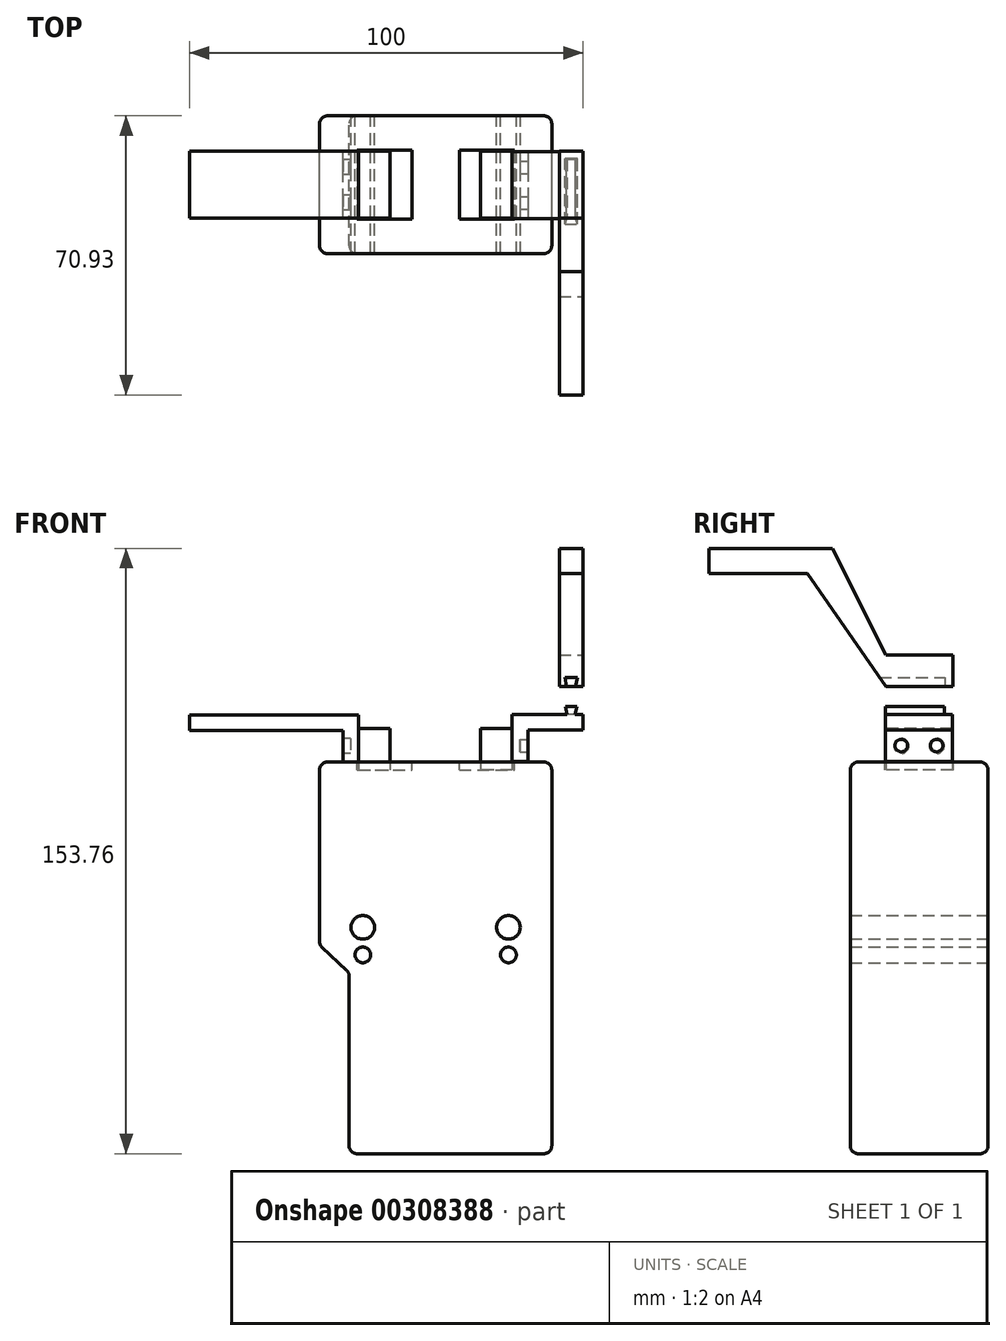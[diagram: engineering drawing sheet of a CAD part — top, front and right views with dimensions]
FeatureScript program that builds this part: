
annotation { "Feature Type Name" : "Feature", "Feature Type Description" : "" }
export const myFeature = defineFeature(function(context is Context, id is Id, definition is map)
    precondition{}
    {
        {
            var Q0;
            Q0=qCreatedBy(makeId("Front.planeOp"),FACE);
            var sketch = newSketch(context, id + "F0", { "sketchPlane" : qUnion([Q0])});
            skLineSegment(sketch, "E0", {"start": v(0, 2) * mm, "end": v(0, 97.5) * mm});
            skLineSegment(sketch, "E1", {"start": v(-2, 99.5) * mm, "end": v(-57, 99.5) * mm});
            skLineSegment(sketch, "E2", {"start": v(-59, 97.5) * mm, "end": v(-59, 53.87) * mm});
            skLineSegment(sketch, "E3", {"start": v(-58.36, 52.4) * mm, "end": v(-52.14, 46.6) * mm});
            skLineSegment(sketch, "E4", {"start": v(-51.5, 45.13) * mm, "end": v(-51.5, 2) * mm});
            skLineSegment(sketch, "E5", {"start": v(-49.5, 0) * mm, "end": v(-2, 0) * mm});
            skCircle(sketch, "E6", {"center": v(-48, 57.5) * mm, "radius": 3 * mm});
            skCircle(sketch, "E7", {"center": v(-48, 50.5) * mm, "radius": 2 * mm});
            skCircle(sketch, "E8", {"center": v(-11, 57.5) * mm, "radius": 3 * mm});
            skCircle(sketch, "E9", {"center": v(-11, 50.5) * mm, "radius": 2 * mm});
            skLineSegment(sketch, "E10", {"start": v(-48, 57.5) * mm, "end": v(-11, 57.5) * mm, "construction": true});
            skLineSegment(sketch, "E11", {"start": v(-48, 50.5) * mm, "end": v(-11, 50.5) * mm, "construction": true});
            skPoint(sketch, "E12.visualSharp", {"position": v(-59, 53) * mm});
            skArc(sketch, "E12.filletArc", {"start": v(-59, 53.87) * mm, "mid": v(-58.83, 53.07) * mm, "end": v(-58.36, 52.4) * mm});
            skPoint(sketch, "E13.visualSharp", {"position": v(-51.5, 46) * mm});
            skArc(sketch, "E13.filletArc", {"start": v(-51.5, 45.13) * mm, "mid": v(-51.67, 45.93) * mm, "end": v(-52.14, 46.6) * mm});
            skPoint(sketch, "E14.visualSharp", {"position": v(-59, 99.5) * mm});
            skArc(sketch, "E14.filletArc", {"start": v(-57, 99.5) * mm, "mid": v(-58.41, 98.91) * mm, "end": v(-59, 97.5) * mm});
            skPoint(sketch, "E15.visualSharp", {"position": v(0, 99.5) * mm});
            skArc(sketch, "E15.filletArc", {"start": v(0, 97.5) * mm, "mid": v(-0.59, 98.91) * mm, "end": v(-2, 99.5) * mm});
            skPoint(sketch, "E16.visualSharp", {"position": v(0, 0) * mm});
            skArc(sketch, "E16.filletArc", {"start": v(-2, 0) * mm, "mid": v(-0.59, 0.59) * mm, "end": v(0, 2) * mm});
            skPoint(sketch, "E17.visualSharp", {"position": v(-51.5, 0) * mm});
            skArc(sketch, "E17.filletArc", {"start": v(-51.5, 2) * mm, "mid": v(-50.91, 0.59) * mm, "end": v(-49.5, 0) * mm});
            skSolve(sketch);
        }
        {
            var Q0;
            Q0=makeQuery(id+"F0.imprint","IMPRINT",FACE,{"disambiguationData":[TD([[makeQuery(id+"F0.imprint","IMPRINT",EDGE,{"derivedFrom":sQuery(id+"F0.wireOp",EDGE,"E0")}),1.0]])]});
            extrude(context, id + "F1", {"entities" : qUnion([Q0]), "depth" : 35 * mm});
        }
        {
            var Q0;
            Q0=makeQuery(id+"F1.opExtrude","CAP_EDGE",EDGE,{"disambiguationData":[OSD([sQuery(id+"F0.wireOp",EDGE,"E0")])],"isStart":true});
            var Q1;
            Q1=makeQuery(id+"F1.opExtrude","CAP_EDGE",EDGE,{"disambiguationData":[OSD([sQuery(id+"F0.wireOp",EDGE,"E1")])],"isStart":false});
            fillet(context, id + "F2", {"entities" : qUnion([Q0, Q1]), "radius" : 2 * mm, "tangentPropagation" : true, "allowEdgeOverflow" : false});
        }
        {
            var Q0;
            Q0=makeQuery(id+"F1.opExtrude","SWEPT_FACE",FACE,{"disambiguationData":[OSD([sQuery(id+"F0.wireOp",EDGE,"E1")])]});
            var sketch = newSketch(context, id + "F3", { "sketchPlane" : qUnion([Q0])});
            skLineSegment(sketch, "E18.bottom", {"start": v(-49.5, -8.75) * mm, "end": v(-35.5, -8.75) * mm});
            skLineSegment(sketch, "E18.top", {"start": v(-49.5, -26.25) * mm, "end": v(-35.5, -26.25) * mm});
            skLineSegment(sketch, "E18.left", {"start": v(-49.5, -8.75) * mm, "end": v(-49.5, -26.25) * mm});
            skLineSegment(sketch, "E18.right", {"start": v(-35.5, -8.75) * mm, "end": v(-35.5, -26.25) * mm});
            skLineSegment(sketch, "E19.bottom", {"start": v(-23.5, -8.75) * mm, "end": v(-9.5, -8.75) * mm});
            skLineSegment(sketch, "E19.top", {"start": v(-23.5, -26.25) * mm, "end": v(-9.5, -26.25) * mm});
            skLineSegment(sketch, "E19.left", {"start": v(-23.5, -8.75) * mm, "end": v(-23.5, -26.25) * mm});
            skLineSegment(sketch, "E19.right", {"start": v(-9.5, -8.75) * mm, "end": v(-9.5, -26.25) * mm});
            skLineSegment(sketch, "E20", {"start": v(-57, -17.5) * mm, "end": v(-2, -17.5) * mm, "construction": true});
            skLineSegment(sketch, "E21", {"start": v(-29.5, -2) * mm, "end": v(-29.5, -33) * mm, "construction": true});
            skLineSegment(sketch, "E22", {"start": v(-29.5, -33) * mm, "end": v(-29.06, -32.58) * mm, "construction": true});
            skPoint(sketch, "E23", {"position": v(-35.5, -17.5) * mm});
            skLineSegment(sketch, "E24", {"start": v(-35.5, -17.5) * mm, "end": v(-29.5, -17.5) * mm, "construction": true});
            skLineSegment(sketch, "E25", {"start": v(-35.5, -8.75) * mm, "end": v(-29.5, -8.75) * mm, "construction": true});
            skLineSegment(sketch, "E26", {"start": v(-29.5, -8.75) * mm, "end": v(-23.5, -8.75) * mm, "construction": true});
            skSolve(sketch);
        }
        {
            var Q0;
            Q0 = qSketchRegion(id + "F3", true);
            extrude(context, id + "F4", {"entities" : qUnion([Q0]), "operationType" : NewBodyOperationType.REMOVE, "oppositeDirection" : true, "depth" : 2 * mm});
        }
        {
            var Q0;
            Q0=makeQuery(id+"F4.boolean.opBoolean","COPY",FACE,{"derivedFrom":makeQuery(id+"F4.opExtrude","CAP_FACE",FACE,{"disambiguationData":[OSD([sQuery(id+"F3.wireOp",EDGE,"E18.bottom"),sQuery(id+"F3.wireOp",EDGE,"E18.top"),sQuery(id+"F3.wireOp",EDGE,"E18.left"),sQuery(id+"F3.wireOp",EDGE,"E18.right")])],"isStart":false})});
            var sketch = newSketch(context, id + "F5", { "sketchPlane" : qUnion([Q0])});
            skLineSegment(sketch, "E27.bottom", {"start": v(-49.08, -9) * mm, "end": v(-41.08, -9) * mm});
            skLineSegment(sketch, "E27.top", {"start": v(-49.08, -26) * mm, "end": v(-41.08, -26) * mm});
            skLineSegment(sketch, "E27.left", {"start": v(-49.08, -9) * mm, "end": v(-49.08, -26) * mm});
            skLineSegment(sketch, "E27.right", {"start": v(-41.08, -9) * mm, "end": v(-41.08, -26) * mm});
            skLineSegment(sketch, "E28.bottom", {"start": v(-10.08, -9) * mm, "end": v(-18.08, -9) * mm});
            skLineSegment(sketch, "E28.top", {"start": v(-10.08, -26) * mm, "end": v(-18.08, -26) * mm});
            skLineSegment(sketch, "E28.left", {"start": v(-10.08, -9) * mm, "end": v(-10.08, -26) * mm});
            skLineSegment(sketch, "E28.right", {"start": v(-18.08, -9) * mm, "end": v(-18.08, -26) * mm});
            skLineSegment(sketch, "E29", {"start": v(-49.08, -17.5) * mm, "end": v(-41.08, -17.5) * mm, "construction": true});
            skLineSegment(sketch, "E30", {"start": v(-41.08, -17.5) * mm, "end": v(-18.08, -17.5) * mm, "construction": true});
            skPoint(sketch, "E31", {"position": v(-49.5, -17.5) * mm});
            skSolve(sketch);
        }
        {
            var Q0;
            Q0 = qSketchRegion(id + "F5", true);
            extrude(context, id + "F6", {"entities" : qUnion([Q0]), "operationType" : NewBodyOperationType.ADD, "depth" : 10.5 * mm});
        }
        {
            var Q0;
            Q0=makeQuery(id+"F6.opExtrude","SWEPT_FACE",FACE,{"disambiguationData":[OSD([sQuery(id+"F5.wireOp",EDGE,"E27.left")])]});
            var sketch = newSketch(context, id + "F7", { "sketchPlane" : qUnion([Q0])});
            skLineSegment(sketch, "E32", {"start": v(9, 103.58) * mm, "end": v(26, 103.58) * mm, "construction": true});
            skLineSegment(sketch, "E33", {"start": v(17.5, 108) * mm, "end": v(17.5, 99.6) * mm, "construction": true});
            skPoint(sketch, "E33.endSnap0", {"position": v(17.5, 108) * mm});
            skCircle(sketch, "E34", {"center": v(13, 103.58) * mm, "radius": 2 * mm});
            skCircle(sketch, "E35", {"center": v(22, 103.58) * mm, "radius": 2 * mm});
            skLineSegment(sketch, "E36", {"start": v(13, 105.58) * mm, "end": v(17.5, 105.58) * mm, "construction": true});
            skLineSegment(sketch, "E37", {"start": v(22, 105.58) * mm, "end": v(17.5, 105.58) * mm, "construction": true});
            skSolve(sketch);
        }
        {
            var Q0;
            Q0 = qSketchRegion(id + "F7", true);
            extrude(context, id + "F8", {"entities" : qUnion([Q0]), "operationType" : NewBodyOperationType.ADD, "depth" : 2 * mm});
        }
        {
            var Q0;
            Q0=makeQuery(id+"F6.opExtrude","SWEPT_FACE",FACE,{"disambiguationData":[OSD([sQuery(id+"F5.wireOp",EDGE,"E28.left")])]});
            var sketch = newSketch(context, id + "F9", { "sketchPlane" : qUnion([Q0])});
            skLineSegment(sketch, "E38", {"start": v(-26, 103.72) * mm, "end": v(-9, 103.72) * mm, "construction": true});
            skLineSegment(sketch, "E39", {"start": v(-17.5, 108) * mm, "end": v(-17.5, 99.5) * mm, "construction": true});
            skPoint(sketch, "E39.endSnap0", {"position": v(-17.5, 103.72) * mm});
            skCircle(sketch, "E40", {"center": v(-22, 103.72) * mm, "radius": 2 * mm});
            skCircle(sketch, "E41", {"center": v(-13, 103.72) * mm, "radius": 2 * mm});
            skLineSegment(sketch, "E42", {"start": v(-22, 105.72) * mm, "end": v(-17.5, 105.72) * mm, "construction": true});
            skLineSegment(sketch, "E43", {"start": v(-13, 105.72) * mm, "end": v(-17.5, 105.72) * mm, "construction": true});
            skSolve(sketch);
        }
        {
            var Q0;
            Q0 = qSketchRegion(id + "F9", true);
            extrude(context, id + "F10", {"entities" : qUnion([Q0]), "operationType" : NewBodyOperationType.ADD, "depth" : 2 * mm});
        }
        {
            var Q0;
            Q0=makeQuery(id+"F6.opExtrude","SWEPT_FACE",FACE,{"disambiguationData":[OSD([sQuery(id+"F5.wireOp",EDGE,"E28.left")])]});
            cPlane(context, id + "F11", {"entities" : qUnion([Q0]), "cplaneType" : CPlaneType.OFFSET, "offset" : 4 * mm, "width" : 150 * mm, "height" : 150 * mm});
        }
        {
            var Q0;
            Q0=qCreatedBy(id+"F11.planeOp",FACE);
            var sketch = newSketch(context, id + "F12", { "sketchPlane" : qUnion([Q0])});
            skLineSegment(sketch, "E44.bottom", {"start": v(-26.07, 99.61) * mm, "end": v(-9.07, 99.61) * mm});
            skLineSegment(sketch, "E44.top", {"start": v(-26.07, 111.61) * mm, "end": v(-9.07, 111.61) * mm});
            skLineSegment(sketch, "E44.left", {"start": v(-26.07, 99.61) * mm, "end": v(-26.07, 111.61) * mm});
            skLineSegment(sketch, "E44.right", {"start": v(-9.07, 99.61) * mm, "end": v(-9.07, 111.61) * mm});
            skCircle(sketch, "E45", {"center": v(-22.07, 103.7) * mm, "radius": 1.59 * mm});
            skCircle(sketch, "E46", {"center": v(-13.07, 103.7) * mm, "radius": 1.59 * mm});
            skLineSegment(sketch, "E47", {"start": v(-26.07, 103.7) * mm, "end": v(-9.07, 103.7) * mm, "construction": true});
            skLineSegment(sketch, "E48", {"start": v(-17.57, 111.61) * mm, "end": v(-17.57, 99.61) * mm, "construction": true});
            skLineSegment(sketch, "E49", {"start": v(-22.07, 105.28) * mm, "end": v(-17.57, 105.28) * mm, "construction": true});
            skLineSegment(sketch, "E50", {"start": v(-13.07, 105.28) * mm, "end": v(-17.57, 105.28) * mm, "construction": true});
            skSolve(sketch);
        }
        {
            var Q0;
            Q0 = qSketchRegion(id + "F12", true);
            extrude(context, id + "F13", {"entities" : qUnion([Q0]), "oppositeDirection" : true, "depth" : 4 * mm});
        }
        {
            var Q0;
            Q0=makeQuery(id+"F13.opExtrude","CAP_FACE",FACE,{"disambiguationData":[OSD([sQuery(id+"F12.wireOp",EDGE,"E44.bottom"),sQuery(id+"F12.wireOp",EDGE,"E44.top"),sQuery(id+"F12.wireOp",EDGE,"E44.left"),sQuery(id+"F12.wireOp",EDGE,"E44.right"),sQuery(id+"F12.wireOp",EDGE,"E45"),sQuery(id+"F12.wireOp",EDGE,"E46")])],"isStart":false});
            var sketch = newSketch(context, id + "F14", { "sketchPlane" : qUnion([Q0])});
            skLineSegment(sketch, "E51.bottom", {"start": v(26.07, 111.61) * mm, "end": v(9.07, 111.61) * mm});
            skLineSegment(sketch, "E51.top", {"start": v(26.07, 107.61) * mm, "end": v(9.07, 107.61) * mm});
            skLineSegment(sketch, "E51.left", {"start": v(26.07, 111.61) * mm, "end": v(26.07, 107.61) * mm});
            skLineSegment(sketch, "E51.right", {"start": v(9.07, 111.61) * mm, "end": v(9.07, 107.61) * mm});
            skSolve(sketch);
        }
        {
            var Q0;
            Q0 = qSketchRegion(id + "F14", true);
            extrude(context, id + "F15", {"entities" : qUnion([Q0]), "operationType" : NewBodyOperationType.ADD, "oppositeDirection" : true, "depth" : 18 * mm});
        }
        {
            var Q0;
            Q0=makeQuery(id+"F6.opExtrude","SWEPT_FACE",FACE,{"disambiguationData":[OSD([sQuery(id+"F5.wireOp",EDGE,"E27.left")])]});
            cPlane(context, id + "F16", {"entities" : qUnion([Q0]), "cplaneType" : CPlaneType.OFFSET, "offset" : 4 * mm, "width" : 150 * mm, "height" : 150 * mm});
        }
        {
            var Q0;
            Q0=qCreatedBy(id+"F16.planeOp",FACE);
            var sketch = newSketch(context, id + "F17", { "sketchPlane" : qUnion([Q0])});
            skLineSegment(sketch, "E52.bottom", {"start": v(26.04, 99.51) * mm, "end": v(9.04, 99.51) * mm});
            skLineSegment(sketch, "E52.top", {"start": v(26.04, 111.51) * mm, "end": v(9.04, 111.51) * mm});
            skLineSegment(sketch, "E52.left", {"start": v(26.04, 99.51) * mm, "end": v(26.04, 111.51) * mm});
            skLineSegment(sketch, "E52.right", {"start": v(9.04, 99.51) * mm, "end": v(9.04, 111.51) * mm});
            skLineSegment(sketch, "E53", {"start": v(9.04, 103.6) * mm, "end": v(26.04, 103.6) * mm, "construction": true});
            skCircle(sketch, "E54", {"center": v(13.04, 103.6) * mm, "radius": 1.9 * mm});
            skCircle(sketch, "E55", {"center": v(22.04, 103.6) * mm, "radius": 1.9 * mm});
            skLineSegment(sketch, "E56", {"start": v(17.54, 103.6) * mm, "end": v(17.54, 111.51) * mm, "construction": true});
            skLineSegment(sketch, "E57", {"start": v(13.04, 105.5) * mm, "end": v(17.54, 105.5) * mm, "construction": true});
            skLineSegment(sketch, "E58", {"start": v(22.04, 105.5) * mm, "end": v(17.54, 105.5) * mm, "construction": true});
            skSolve(sketch);
        }
        {
            var Q0;
            Q0 = qSketchRegion(id + "F17", true);
            extrude(context, id + "F18", {"entities" : qUnion([Q0]), "oppositeDirection" : true, "depth" : 4 * mm});
        }
        {
            var Q0;
            Q0=makeQuery(id+"F18.opExtrude","CAP_FACE",FACE,{"disambiguationData":[OSD([sQuery(id+"F17.wireOp",EDGE,"E52.bottom"),sQuery(id+"F17.wireOp",EDGE,"E52.top"),sQuery(id+"F17.wireOp",EDGE,"E52.left"),sQuery(id+"F17.wireOp",EDGE,"E52.right"),sQuery(id+"F17.wireOp",EDGE,"E54"),sQuery(id+"F17.wireOp",EDGE,"E55")])],"isStart":false});
            var sketch = newSketch(context, id + "F19", { "sketchPlane" : qUnion([Q0])});
            skLineSegment(sketch, "E59.bottom", {"start": v(-26.04, 107.51) * mm, "end": v(-9.04, 107.51) * mm});
            skLineSegment(sketch, "E59.top", {"start": v(-26.04, 111.51) * mm, "end": v(-9.04, 111.51) * mm});
            skLineSegment(sketch, "E59.left", {"start": v(-26.04, 107.51) * mm, "end": v(-26.04, 111.51) * mm});
            skLineSegment(sketch, "E59.right", {"start": v(-9.04, 107.51) * mm, "end": v(-9.04, 111.51) * mm});
            skSolve(sketch);
        }
        {
            var Q0;
            Q0 = qSketchRegion(id + "F19", true);
            extrude(context, id + "F20", {"entities" : qUnion([Q0]), "operationType" : NewBodyOperationType.ADD, "oppositeDirection" : true, "depth" : 43 * mm});
        }
        {
            var Q0;
            Q0=makeQuery(id+"F15.boolean.opBoolean","MERGE",FACE,{"derivedFrom":[makeQuery(id+"F13.opExtrude","SWEPT_FACE",FACE,{"disambiguationData":[OSD([sQuery(id+"F12.wireOp",EDGE,"E44.left")])]}),makeQuery(id+"F15.opExtrude","SWEPT_FACE",FACE,{"disambiguationData":[OSD([sQuery(id+"F14.wireOp",EDGE,"E51.left")])]})]});
            var sketch = newSketch(context, id + "F21", { "sketchPlane" : qUnion([Q0])});
            skLineSegment(sketch, "E60", {"start": v(3.92, 111.61) * mm, "end": v(3.42, 113.61) * mm});
            skLineSegment(sketch, "E61", {"start": v(3.42, 113.61) * mm, "end": v(6.42, 113.61) * mm});
            skLineSegment(sketch, "E62", {"start": v(6.42, 113.61) * mm, "end": v(5.92, 111.61) * mm});
            skLineSegment(sketch, "E63", {"start": v(5.92, 111.61) * mm, "end": v(3.92, 111.61) * mm});
            skLineSegment(sketch, "E64", {"start": v(4.92, 107.61) * mm, "end": v(4.92, 113.61) * mm, "construction": true});
            skPoint(sketch, "E65", {"position": v(4.92, 113.61) * mm});
            skPoint(sketch, "E66", {"position": v(4.92, 111.61) * mm});
            skSolve(sketch);
        }
        {
            var Q0;
            Q0 = qSketchRegion(id + "F21", true);
            var Q1;
            Q1=makeQuery(id+"F15.boolean.opBoolean","MERGE",FACE,{"derivedFrom":[makeQuery(id+"F13.opExtrude","SWEPT_FACE",FACE,{"disambiguationData":[OSD([sQuery(id+"F12.wireOp",EDGE,"E44.right")])]}),makeQuery(id+"F15.opExtrude","SWEPT_FACE",FACE,{"disambiguationData":[OSD([sQuery(id+"F14.wireOp",EDGE,"E51.right")])]})]});
            extrude(context, id + "F22", {"entities" : qUnion([Q0]), "operationType" : NewBodyOperationType.ADD, "endBound" : BoundingType.UP_TO_SURFACE, "oppositeDirection" : true, "endBoundEntityFace" : qUnion([Q1]), "depth" : 25 * mm});
        }
        {
            var Q0;
            Q0=makeQuery(id+"F15.opExtrude","CAP_FACE",FACE,{"disambiguationData":[OSD([sQuery(id+"F14.wireOp",EDGE,"E51.bottom"),sQuery(id+"F14.wireOp",EDGE,"E51.top"),sQuery(id+"F14.wireOp",EDGE,"E51.left"),sQuery(id+"F14.wireOp",EDGE,"E51.right")])],"isStart":false});
            cPlane(context, id + "F23", {"entities" : qUnion([Q0]), "cplaneType" : CPlaneType.OFFSET, "offset" : 0 * mm, "width" : 150 * mm, "height" : 150 * mm});
        }
        {
            var Q0;
            Q0=qCreatedBy(id+"F23.planeOp",FACE);
            var sketch = newSketch(context, id + "F24", { "sketchPlane" : qUnion([Q0])});
            skLineSegment(sketch, "E67", {"start": v(-25.93, 118.76) * mm, "end": v(-8.93, 118.76) * mm});
            skLineSegment(sketch, "E68", {"start": v(-8.93, 118.76) * mm, "end": v(-8.93, 126.76) * mm});
            skLineSegment(sketch, "E69", {"start": v(-8.93, 126.76) * mm, "end": v(-25.93, 126.76) * mm});
            skLineSegment(sketch, "E70", {"start": v(-25.93, 126.76) * mm, "end": v(-39.58, 153.76) * mm});
            skLineSegment(sketch, "E71", {"start": v(-39.58, 153.76) * mm, "end": v(-70.93, 153.76) * mm});
            skLineSegment(sketch, "E72", {"start": v(-70.93, 153.76) * mm, "end": v(-70.93, 147.4) * mm});
            skLineSegment(sketch, "E73", {"start": v(-70.93, 147.4) * mm, "end": v(-45.93, 147.4) * mm});
            skLineSegment(sketch, "E74", {"start": v(-45.93, 147.4) * mm, "end": v(-25.93, 118.76) * mm});
            skLineSegment(sketch, "E75", {"start": v(-45.93, 147.4) * mm, "end": v(-39.58, 153.76) * mm, "construction": true});
            skSolve(sketch);
        }
        {
            var Q0;
            Q0 = qSketchRegion(id + "F24", true);
            extrude(context, id + "F25", {"entities" : qUnion([Q0]), "oppositeDirection" : true, "depth" : 6 * mm});
        }
        {
            var Q0;
            Q0=makeQuery(id+"F25.opExtrude","SWEPT_FACE",FACE,{"disambiguationData":[OSD([sQuery(id+"F24.wireOp",EDGE,"E68")])]});
            var sketch = newSketch(context, id + "F26", { "sketchPlane" : qUnion([Q0])});
            skLineSegment(sketch, "E76", {"start": v(-6.05, 118.76) * mm, "end": v(-6.55, 121) * mm});
            skLineSegment(sketch, "E77", {"start": v(-6.55, 121) * mm, "end": v(-3.3, 121) * mm});
            skLineSegment(sketch, "E78", {"start": v(-3.3, 121) * mm, "end": v(-3.8, 118.76) * mm});
            skPoint(sketch, "E79", {"position": v(-4.92, 118.76) * mm});
            skLineSegment(sketch, "E80", {"start": v(-4.92, 118.76) * mm, "end": v(-4.92, 121) * mm, "construction": true});
            skSolve(sketch);
        }
        {
            var Q0;
            {var subQ0=sQuery(id+"F26.wireOp",EDGE,"E76");Q0=makeQuery(id+"F26.imprint","IMPRINT",FACE,{"disambiguationData":[TD([[makeQuery(id+"F26.imprint","IMPRINT",EDGE,{"derivedFrom":subQ0}),-1.0]])]});}
            extrude(context, id + "F27", {"entities" : qUnion([Q0]), "operationType" : NewBodyOperationType.REMOVE, "endBound" : BoundingType.THROUGH_ALL, "oppositeDirection" : true, "depth" : 15 * mm});
        }
        {
            var Q0;
            Q0=makeQuery(id+"F25.opExtrude","SWEPT_FACE",FACE,{"disambiguationData":[OSD([sQuery(id+"F24.wireOp",EDGE,"E68")])]});
            var sketch = newSketch(context, id + "F28", { "sketchPlane" : qUnion([Q0])});
            skLineSegment(sketch, "E81.bottom", {"start": v(-7.92, 118.76) * mm, "end": v(-1.92, 118.76) * mm});
            skLineSegment(sketch, "E81.top", {"start": v(-7.92, 126.76) * mm, "end": v(-1.92, 126.76) * mm});
            skLineSegment(sketch, "E81.left", {"start": v(-7.92, 118.76) * mm, "end": v(-7.92, 126.76) * mm});
            skLineSegment(sketch, "E81.right", {"start": v(-1.92, 118.76) * mm, "end": v(-1.92, 126.76) * mm});
            skSolve(sketch);
        }
        {
            var Q0;
            Q0 = qSketchRegion(id + "F28", true);
            extrude(context, id + "F29", {"entities" : qUnion([Q0]), "operationType" : NewBodyOperationType.ADD, "oppositeDirection" : true, "depth" : 2 * mm});
        }
        {
            var Q0;
            {var subQ0=sQuery(id+"F14.wireOp",EDGE,"E51.right");var subQ1=sQuery(id+"F12.wireOp",EDGE,"E44.right");Q0=makeQuery(id+"F22.boolean.opBoolean","MERGE",FACE,{"derivedFrom":[makeQuery(id+"F15.boolean.opBoolean","MERGE",FACE,{"derivedFrom":[makeQuery(id+"F13.opExtrude","SWEPT_FACE",FACE,{"disambiguationData":[OSD([subQ1])]}),makeQuery(id+"F15.opExtrude","SWEPT_FACE",FACE,{"disambiguationData":[OSD([subQ0])]})]}),makeQuery(id+"F22.opExtrude","CAP_FACE",FACE,{"disambiguationData":[OSD([subQ1,subQ0])],"isStart":false})]});}
            var sketch = newSketch(context, id + "F30", { "sketchPlane" : qUnion([Q0])});
            skLineSegment(sketch, "E82.bottom", {"start": v(-7.92, 111.61) * mm, "end": v(-1.5, 111.61) * mm});
            skLineSegment(sketch, "E82.top", {"start": v(-7.92, 114.03) * mm, "end": v(-1.5, 114.03) * mm});
            skLineSegment(sketch, "E82.left", {"start": v(-7.92, 111.61) * mm, "end": v(-7.92, 114.03) * mm});
            skLineSegment(sketch, "E82.right", {"start": v(-1.5, 111.61) * mm, "end": v(-1.5, 114.03) * mm});
            skSolve(sketch);
        }
        {
            var Q0;
            Q0 = qSketchRegion(id + "F30", true);
            extrude(context, id + "F31", {"entities" : qUnion([Q0]), "operationType" : NewBodyOperationType.REMOVE, "oppositeDirection" : true, "depth" : 2 * mm});
        }
    });
